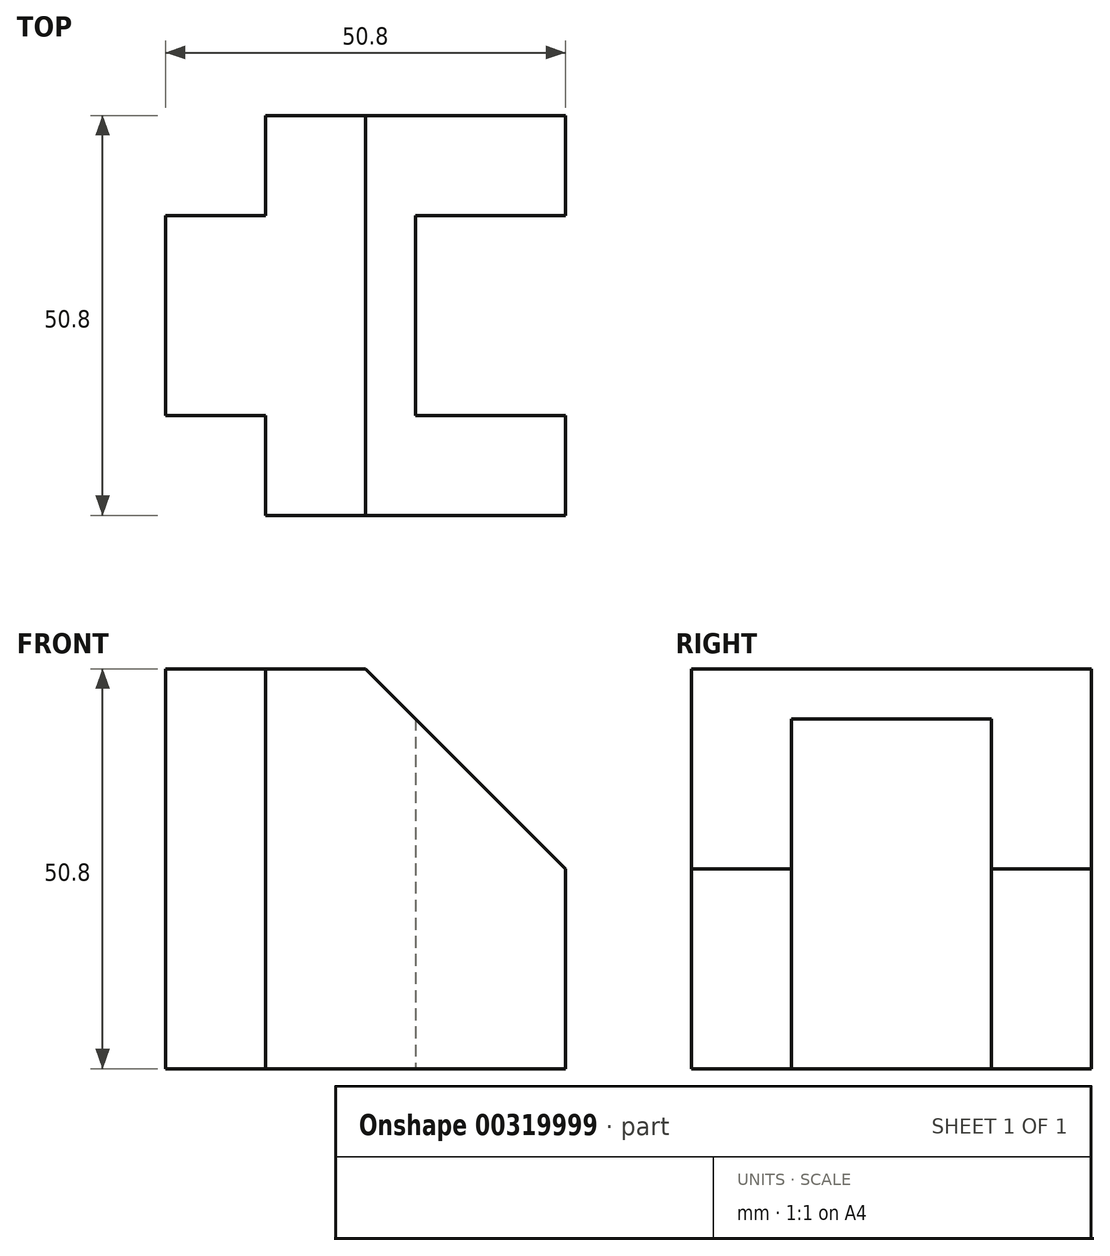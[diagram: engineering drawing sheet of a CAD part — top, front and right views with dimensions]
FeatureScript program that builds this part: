
annotation { "Feature Type Name" : "Feature", "Feature Type Description" : "" }
export const myFeature = defineFeature(function(context is Context, id is Id, definition is map)
    precondition{}
    {
        {
            var Q0;
            Q0=qCreatedBy(makeId("Top.planeOp"),FACE);
            var sketch = newSketch(context, id + "F0", { "sketchPlane" : qUnion([Q0])});
            skLineSegment(sketch, "E0", {"start": v(0, 0) * mm, "end": v(0, 50.8) * mm});
            skLineSegment(sketch, "E1", {"start": v(0, 50.8) * mm, "end": v(25.4, 50.8) * mm});
            skLineSegment(sketch, "E2", {"start": v(25.4, 50.8) * mm, "end": v(25.4, 38.1) * mm});
            skLineSegment(sketch, "E3", {"start": v(25.4, 38.1) * mm, "end": v(6.35, 38.1) * mm});
            skLineSegment(sketch, "E4", {"start": v(6.35, 38.1) * mm, "end": v(6.35, 12.7) * mm});
            skLineSegment(sketch, "E5", {"start": v(6.35, 12.7) * mm, "end": v(25.4, 12.7) * mm});
            skLineSegment(sketch, "E6", {"start": v(25.4, 12.7) * mm, "end": v(25.4, 0) * mm});
            skLineSegment(sketch, "E7", {"start": v(25.4, 0) * mm, "end": v(0, 0) * mm});
            skLineSegment(sketch, "E8", {"start": v(0, 0) * mm, "end": v(-12.7, 0) * mm});
            skLineSegment(sketch, "E9", {"start": v(-12.7, 0) * mm, "end": v(-12.7, 12.7) * mm});
            skLineSegment(sketch, "E10", {"start": v(-12.7, 12.7) * mm, "end": v(-25.4, 12.7) * mm});
            skLineSegment(sketch, "E11", {"start": v(-25.4, 12.7) * mm, "end": v(-25.4, 38.1) * mm});
            skLineSegment(sketch, "E12", {"start": v(-25.4, 38.1) * mm, "end": v(-12.7, 38.1) * mm});
            skLineSegment(sketch, "E13", {"start": v(-12.7, 38.1) * mm, "end": v(-12.7, 50.8) * mm});
            skLineSegment(sketch, "E14", {"start": v(-12.7, 50.8) * mm, "end": v(0, 50.8) * mm});
            skSolve(sketch);
        }
        {
            var Q0;
            Q0 = qSketchRegion(id + "F0", true);
            extrude(context, id + "F1", {"entities" : qUnion([Q0]), "depth" : 50.8 * mm});
        }
        {
            var Q0;
            Q0=makeQuery(id+"F1.opExtrude","SWEPT_FACE",FACE,{"disambiguationData":[OSD([sQuery(id+"F0.wireOp",EDGE,"E7"),sQuery(id+"F0.wireOp",EDGE,"E8")])]});
            var sketch = newSketch(context, id + "F2", { "sketchPlane" : qUnion([Q0])});
            skLineSegment(sketch, "E15", {"start": v(0, 50.8) * mm, "end": v(25.4, 25.4) * mm});
            skSolve(sketch);
        }
        {
            var Q0;
            {var subQ0=sQuery(id+"F2.wireOp",EDGE,"E15");Q0=makeQuery(id+"F2.imprint","IMPRINT",FACE,{"disambiguationData":[TD([[makeQuery(id+"F2.imprint","IMPRINT",EDGE,{"derivedFrom":subQ0}),1.0]])]});}
            extrude(context, id + "F3", {"entities" : qUnion([Q0]), "operationType" : NewBodyOperationType.REMOVE, "endBound" : BoundingType.THROUGH_ALL, "oppositeDirection" : true, "depth" : 25.4 * mm});
        }
    });
